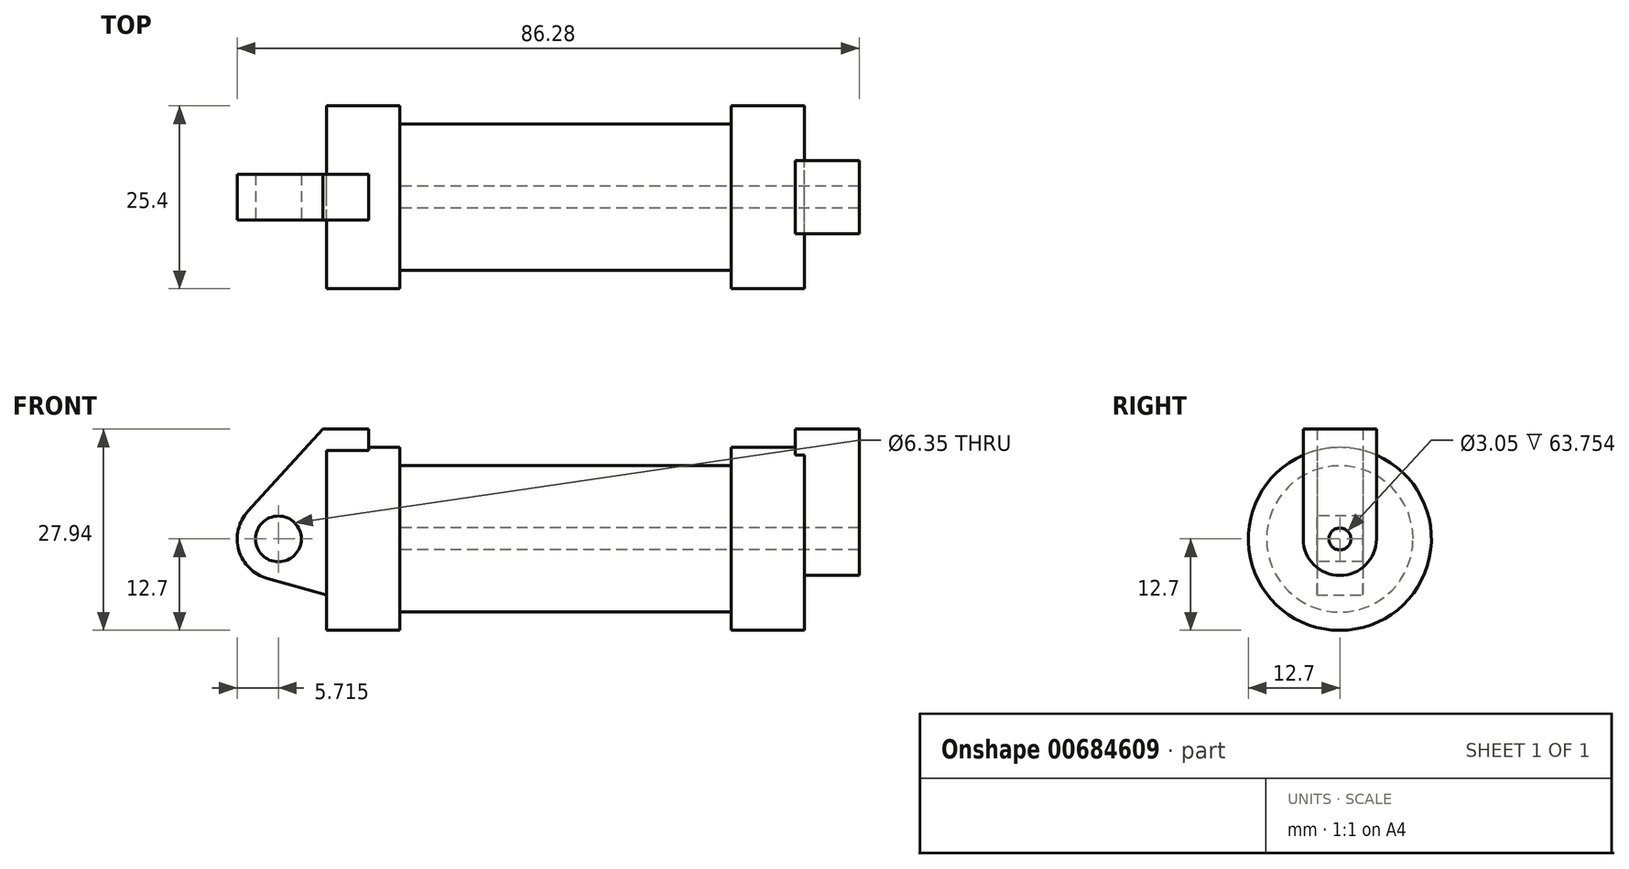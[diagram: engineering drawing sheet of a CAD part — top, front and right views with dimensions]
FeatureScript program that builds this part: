
annotation { "Feature Type Name" : "Feature", "Feature Type Description" : "" }
export const myFeature = defineFeature(function(context is Context, id is Id, definition is map)
    precondition{}
    {
        {
            var Q0;
            Q0=qCreatedBy(makeId("Front.planeOp"),FACE);
            var sketch = newSketch(context, id + "F0", { "sketchPlane" : qUnion([Q0])});
            skLineSegment(sketch, "E0", {"start": v(0, 0) * mm, "end": v(0, 12.7) * mm});
            skLineSegment(sketch, "E1", {"start": v(0, 12.7) * mm, "end": v(10.16, 12.7) * mm});
            skLineSegment(sketch, "E2", {"start": v(10.16, 12.7) * mm, "end": v(10.16, 10.16) * mm});
            skLineSegment(sketch, "E3", {"start": v(10.16, 10.16) * mm, "end": v(56.13, 10.16) * mm});
            skLineSegment(sketch, "E4", {"start": v(56.13, 10.16) * mm, "end": v(56.13, 12.7) * mm});
            skLineSegment(sketch, "E5", {"start": v(56.13, 12.7) * mm, "end": v(66.3, 12.7) * mm});
            skLineSegment(sketch, "E6", {"start": v(66.3, 12.7) * mm, "end": v(66.3, 0) * mm});
            skLineSegment(sketch, "E7", {"start": v(66.3, 0) * mm, "end": v(0, 0) * mm});
            skLineSegment(sketch, "E8", {"start": v(5.84, 15.24) * mm, "end": v(-0.5, 15.24) * mm});
            skLineSegment(sketch, "E9", {"start": v(-0.5, 15.24) * mm, "end": v(-10.88, 3.85) * mm});
            skLineSegment(sketch, "E10", {"start": v(0, 0) * mm, "end": v(-6.65, 0) * mm});
            skCircle(sketch, "E11", {"center": v(-6.65, 0) * mm, "radius": 5.72 * mm});
            skCircle(sketch, "E12", {"center": v(-6.65, 0) * mm, "radius": 3.18 * mm});
            skLineSegment(sketch, "E13", {"start": v(5.84, 15.24) * mm, "end": v(5.84, -9.4) * mm});
            skLineSegment(sketch, "E14", {"start": v(5.84, -9.4) * mm, "end": v(-8.18, -5.5) * mm});
            skSolve(sketch);
        }
        {
            var Q0;
            {var subQ0=sQuery(id+"F0.wireOp",EDGE,"E0");Q0=makeQuery(id+"F0.imprint","IMPRINT",FACE,{"disambiguationData":[TD([[makeQuery(id+"F0.imprint","IMPRINT",EDGE,{"derivedFrom":subQ0}),-1.0]])]});}
            var Q1;
            {var subQ0=sQuery(id+"F0.wireOp",EDGE,"E2");Q1=makeQuery(id+"F0.imprint","IMPRINT",FACE,{"disambiguationData":[TD([[makeQuery(id+"F0.imprint","IMPRINT",EDGE,{"derivedFrom":subQ0}),-1.0]])]});}
            var Q2;
            Q2=sQuery(id+"F0.wireOp",EDGE,"E7");
            revolve(context, id + "F1", {"entities" : qUnion([Q0, Q1]), "axis" : qUnion([Q2]), "revolveType" : RevolveType.FULL});
        }
        {
            var Q0;
            {var subQ0=sQuery(id+"F0.wireOp",EDGE,"E12");Q0=makeQuery(id+"F0.imprint","IMPRINT",FACE,{"disambiguationData":[TD([[makeQuery(id+"F0.imprint","IMPRINT",EDGE,{"derivedFrom":subQ0}),1.0]])]});}
            var Q1;
            {var subQ0=sQuery(id+"F0.wireOp",EDGE,"E0");Q1=makeQuery(id+"F0.imprint","IMPRINT",FACE,{"disambiguationData":[TD([[makeQuery(id+"F0.imprint","IMPRINT",EDGE,{"derivedFrom":subQ0}),-1.0]])]});}
            var Q2;
            {var subQ1=sQuery(id+"F0.wireOp",EDGE,"E0");Q2=makeQuery(id+"F0.imprint","IMPRINT",FACE,{"disambiguationData":[TD([[makeQuery(id+"F0.imprint","IMPRINT",EDGE,{"derivedFrom":subQ1}),1.0]])]});}
            var Q3;
            {var subQ0=sQuery(id+"F0.wireOp",EDGE,"E14");Q3=makeQuery(id+"F0.imprint","IMPRINT",FACE,{"disambiguationData":[TD([[makeQuery(id+"F0.imprint","IMPRINT",EDGE,{"derivedFrom":subQ0}),-1.0]])]});}
            var Q4;
            {var subQ5=sQuery(id+"F0.wireOp",EDGE,"E12");Q4=makeQuery(id+"F0.imprint","IMPRINT",FACE,{"disambiguationData":[TD([[makeQuery(id+"F0.imprint","IMPRINT",EDGE,{"derivedFrom":subQ5}),-1.0]])]});}
            extrude(context, id + "F2", {"entities" : qUnion([Q0, Q1, Q2, Q3, Q4]), "operationType" : NewBodyOperationType.ADD, "endBound" : BoundingType.SYMMETRIC, "depth" : 6.35 * mm, "offsetDistance" : 25.4 * mm});
        }
        {
            var Q0;
            {var subQ0=sQuery(id+"F0.wireOp",EDGE,"E12");Q0=makeQuery(id+"F0.imprint","IMPRINT",FACE,{"disambiguationData":[TD([[makeQuery(id+"F0.imprint","IMPRINT",EDGE,{"derivedFrom":subQ0}),1.0]])]});}
            extrude(context, id + "F3", {"entities" : qUnion([Q0]), "operationType" : NewBodyOperationType.REMOVE, "endBound" : BoundingType.SYMMETRIC, "oppositeDirection" : true, "depth" : 6.35 * mm, "offsetDistance" : 25.4 * mm});
        }
        {
            var Q0;
            Q0=makeQuery(id+"F1.opRevolve","SWEPT_FACE",FACE,{"disambiguationData":[OSD([sQuery(id+"F0.wireOp",EDGE,"E6")])]});
            var sketch = newSketch(context, id + "F4", { "sketchPlane" : qUnion([Q0])});
            skCircle(sketch, "E15", {"center": v(0, 0) * mm, "radius": 1.52 * mm});
            skCircle(sketch, "E16", {"center": v(0, 0) * mm, "radius": 5.08 * mm});
            skLineSegment(sketch, "E17", {"start": v(0, 0) * mm, "end": v(-5.08, 0) * mm, "construction": true});
            skLineSegment(sketch, "E18", {"start": v(0, 0) * mm, "end": v(5.08, 0) * mm, "construction": true});
            skLineSegment(sketch, "E19", {"start": v(-5.08, 0) * mm, "end": v(-5.08, 15.24) * mm});
            skLineSegment(sketch, "E20", {"start": v(5.08, 0) * mm, "end": v(5.08, 15.24) * mm});
            skLineSegment(sketch, "E21", {"start": v(5.08, 15.24) * mm, "end": v(-5.08, 15.24) * mm});
            skSolve(sketch);
        }
        {
            var Q0;
            Q0 = qSketchRegion(id + "F4", true);
            extrude(context, id + "F5", {"entities" : qUnion([Q0]), "operationType" : NewBodyOperationType.ADD, "depth" : 7.62 * mm, "offsetDistance" : 25.4 * mm});
        }
        {
            var Q0;
            Q0=makeQuery(id+"F5.opExtrude","CAP_FACE",FACE,{"disambiguationData":[OSD([sQuery(id+"F4.wireOp",EDGE,"E15"),sQuery(id+"F4.wireOp",EDGE,"E16"),sQuery(id+"F4.wireOp",EDGE,"E19"),sQuery(id+"F4.wireOp",EDGE,"E20"),sQuery(id+"F4.wireOp",EDGE,"E21")])],"isStart":true});
            extrude(context, id + "F6", {"entities" : qUnion([Q0]), "operationType" : NewBodyOperationType.ADD, "depth" : 1.27 * mm, "offsetDistance" : 25.4 * mm});
        }
        {
            var Q0;
            Q0=makeQuery(id+"F4.imprint","IMPRINT",FACE,{"disambiguationData":[TD([[makeQuery(id+"F4.imprint","IMPRINT",EDGE,{"derivedFrom":sQuery(id+"F4.wireOp",EDGE,"E15")}),1.0]])]});
            var Q1;
            Q1=makeQuery(id+"F1.opRevolve","SWEPT_FACE",FACE,{"disambiguationData":[OSD([sQuery(id+"F0.wireOp",EDGE,"E2")])]});
            extrude(context, id + "F7", {"entities" : qUnion([Q0]), "operationType" : NewBodyOperationType.REMOVE, "endBound" : BoundingType.UP_TO_SURFACE, "oppositeDirection" : true, "depth" : 66.3 * mm, "endBoundEntityFace" : qUnion([Q1]), "offsetDistance" : 25.4 * mm});
        }
    });
